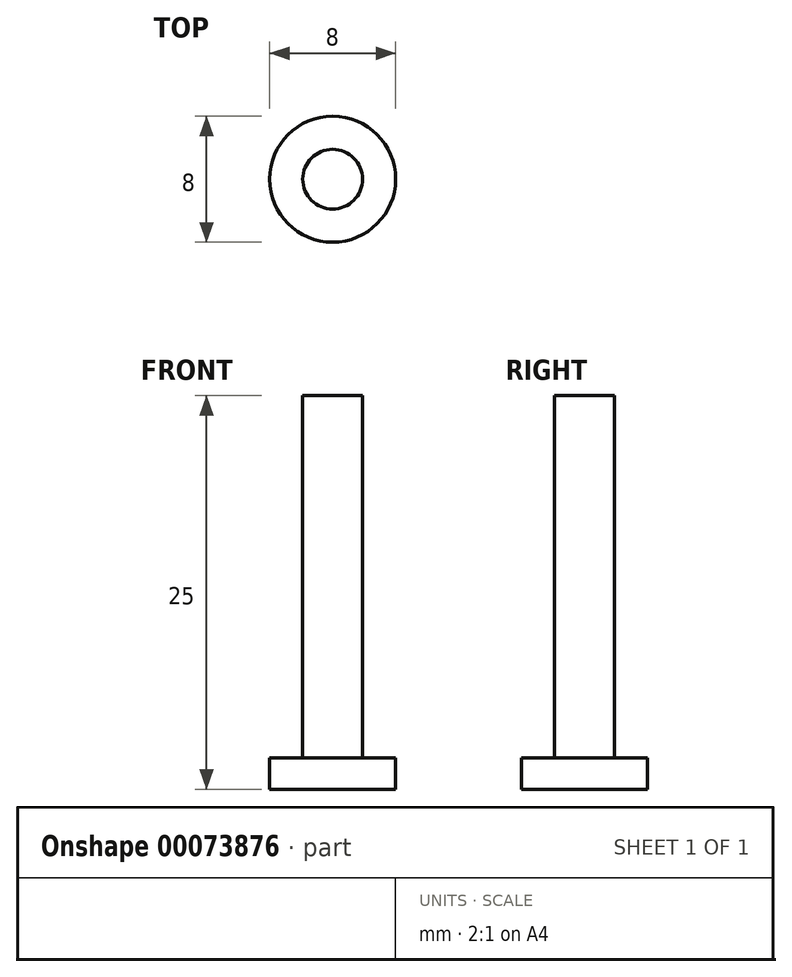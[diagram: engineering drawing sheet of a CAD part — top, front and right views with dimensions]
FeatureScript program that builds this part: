
annotation { "Feature Type Name" : "Feature", "Feature Type Description" : "" }
export const myFeature = defineFeature(function(context is Context, id is Id, definition is map)
    precondition{}
    {
        {
            var Q0;
            Q0=qCreatedBy(makeId("Top.planeOp"),FACE);
            var sketch = newSketch(context, id + "F0", { "sketchPlane" : qUnion([Q0])});
            skCircle(sketch, "E0", {"center": v(0, 0) * mm, "radius": 1.9 * mm});
            skCircle(sketch, "E1", {"center": v(0, 0) * mm, "radius": 4 * mm});
            skSolve(sketch);
        }
        {
            var Q0;
            Q0 = qSketchRegion(id + "F0", true);
            var Q1;
            Q1=makeQuery(id+"F0.imprint","IMPRINT",FACE,{"disambiguationData":[TD([[makeQuery(id+"F0.imprint","IMPRINT",EDGE,{"derivedFrom":sQuery(id+"F0.wireOp",EDGE,"E0")}),1.0]])]});
            extrude(context, id + "F1", {"entities" : qUnion([Q0, Q1]), "depth" : 2 * mm});
        }
        {
            var Q0;
            Q0=makeQuery(id+"F0.imprint","IMPRINT",FACE,{"disambiguationData":[TD([[makeQuery(id+"F0.imprint","IMPRINT",EDGE,{"derivedFrom":sQuery(id+"F0.wireOp",EDGE,"E0")}),1.0]])]});
            extrude(context, id + "F2", {"entities" : qUnion([Q0]), "operationType" : NewBodyOperationType.ADD, "depth" : 25 * mm});
        }
    });
